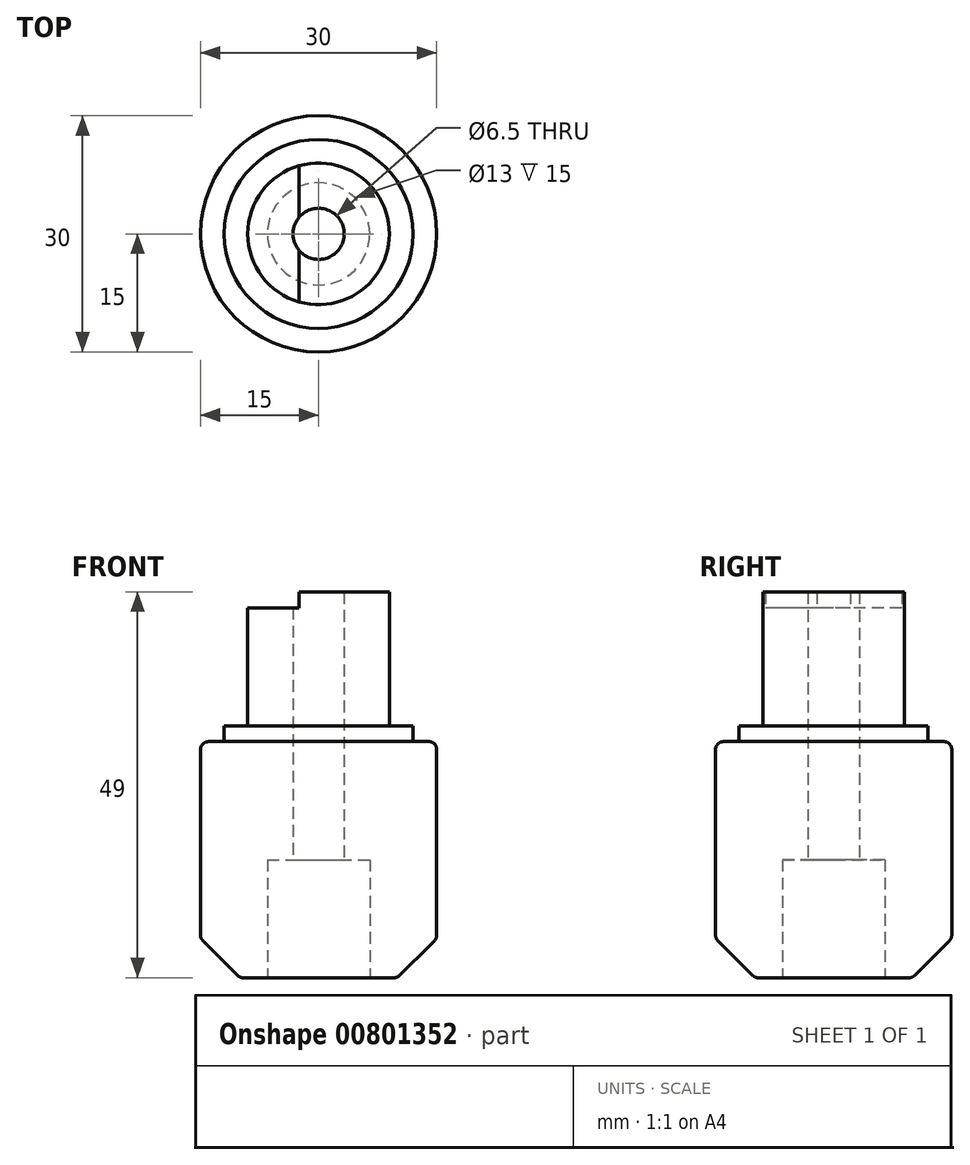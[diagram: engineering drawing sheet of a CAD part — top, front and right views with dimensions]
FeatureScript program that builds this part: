
annotation { "Feature Type Name" : "Feature", "Feature Type Description" : "" }
export const myFeature = defineFeature(function(context is Context, id is Id, definition is map)
    precondition{}
    {
        {
            var Q0;
            Q0=qCreatedBy(makeId("Top.planeOp"),FACE);
            var sketch = newSketch(context, id + "F0", { "sketchPlane" : qUnion([Q0])});
            skCircle(sketch, "E0", {"center": v(0, 0) * mm, "radius": 15 * mm});
            skSolve(sketch);
        }
        {
            var Q0;
            Q0=makeQuery(id+"F0.imprint","IMPRINT",FACE,{"disambiguationData":[TD([[makeQuery(id+"F0.imprint","IMPRINT",EDGE,{"derivedFrom":sQuery(id+"F0.wireOp",EDGE,"E0")}),1.0]])]});
            extrude(context, id + "F1", {"entities" : qUnion([Q0]), "depth" : 30 * mm, "offsetDistance" : 25 * mm});
        }
        {
            var Q0;
            Q0=makeQuery(id+"F1.opExtrude","CAP_FACE",FACE,{"disambiguationData":[OSD([sQuery(id+"F0.wireOp",EDGE,"E0")])],"isStart":false});
            var sketch = newSketch(context, id + "F2", { "sketchPlane" : qUnion([Q0])});
            skCircle(sketch, "E1", {"center": v(0, 0) * mm, "radius": 12 * mm});
            skSolve(sketch);
        }
        {
            var Q0;
            Q0=makeQuery(id+"F2.imprint","IMPRINT",FACE,{"disambiguationData":[TD([[makeQuery(id+"F2.imprint","IMPRINT",EDGE,{"derivedFrom":sQuery(id+"F2.wireOp",EDGE,"E1")}),1.0]])]});
            extrude(context, id + "F3", {"entities" : qUnion([Q0]), "operationType" : NewBodyOperationType.ADD, "depth" : 2 * mm, "offsetDistance" : 25 * mm});
        }
        {
            var Q0;
            Q0=makeQuery(id+"F3.opExtrude","CAP_FACE",FACE,{"disambiguationData":[OSD([sQuery(id+"F2.wireOp",EDGE,"E1")])],"isStart":false});
            var sketch = newSketch(context, id + "F4", { "sketchPlane" : qUnion([Q0])});
            skCircle(sketch, "E2", {"center": v(0, 0) * mm, "radius": 9 * mm});
            skLineSegment(sketch, "E3", {"start": v(-2.47, 8.66) * mm, "end": v(-2.47, -8.66) * mm});
            skSolve(sketch);
        }
        {
            var Q0;
            {var subQ0=sQuery(id+"F4.wireOp",EDGE,"E3");Q0=makeQuery(id+"F4.imprint","IMPRINT",FACE,{"disambiguationData":[TD([[makeQuery(id+"F4.imprint","IMPRINT",EDGE,{"derivedFrom":subQ0}),1.0]])]});}
            extrude(context, id + "F5", {"entities" : qUnion([Q0]), "operationType" : NewBodyOperationType.ADD, "depth" : 17 * mm, "offsetDistance" : 25 * mm});
        }
        {
            var Q0;
            {var subQ0=sQuery(id+"F4.wireOp",EDGE,"E3");Q0=makeQuery(id+"F4.imprint","IMPRINT",FACE,{"disambiguationData":[TD([[makeQuery(id+"F4.imprint","IMPRINT",EDGE,{"derivedFrom":subQ0}),-1.0]])]});}
            extrude(context, id + "F6", {"entities" : qUnion([Q0]), "operationType" : NewBodyOperationType.ADD, "depth" : 15 * mm, "offsetDistance" : 25 * mm});
        }
        {
            var Q0;
            Q0=sQuery(id+"F0.wireOp",VERTEX,"E0.center");
            var Q1;
            Q1=makeQuery(id+"F1.opExtrude","SWEPT_BODY",BODY,{"disambiguationData":[OSD([sQuery(id+"F0.wireOp",EDGE,"E0")])]});
            hole(context, id + "F7", {"style" : HoleStyle.C_BORE, "endStyle" : HoleEndStyle.THROUGH, "oppositeDirection" : true, "holeDiameter" : 6.5 * mm, "cBoreDiameter" : 13 * mm, "cBoreDepth" : 15 * mm, "majorDiameter" : 5 * mm, "isTappedThrough" : true, "tappedDepth" : 12 * mm, "tapClearance" : 3, "locations" : qUnion([Q0]), "scope" : qUnion([Q1])});
        }
        {
            var Q0;
            Q0=makeQuery(id+"F1.opExtrude","CAP_EDGE",EDGE,{"disambiguationData":[OSD([sQuery(id+"F0.wireOp",EDGE,"E0")])],"isStart":true});
            chamfer(context, id + "F8", {"entities" : qUnion([Q0]), "width" : 5 * mm, "tangentPropagation" : true});
        }
        {
            var Q0;
            Q0=makeQuery(id+"F7.hole-0.boolean.opBoolean","COPY",EDGE,{"derivedFrom":makeQuery(id+"F7.hole-0.opRevolve","SWEPT_EDGE",EDGE,{"disambiguationData":[OSD([sQuery(id+"F7.hole-0.sketch.wireOp",EDGE,"cbore_start_line_2"),sQuery(id+"F7.hole-0.sketch.wireOp",EDGE,"cbore_start_line_3")])]})});
            var Q1;
            Q1=makeQuery(id+"F1.opExtrude","CAP_EDGE",EDGE,{"disambiguationData":[OSD([sQuery(id+"F0.wireOp",EDGE,"E0")])],"isStart":false});
            var Q2;
            {var subQ0=sQuery(id+"F0.wireOp",EDGE,"E0");Q2=makeQuery(id+"F8.opChamfer","BLEND_EDGE",EDGE,{"blendedFrom":[makeQuery(id+"F1.opExtrude","CAP_EDGE",EDGE,{"disambiguationData":[OSD([subQ0])],"isStart":true}),makeQuery(id+"F1.opExtrude","CAP_FACE",FACE,{"disambiguationData":[OSD([subQ0])],"isStart":true})],"blendedInto":[makeQuery(id+"F1.opExtrude","CAP_FACE",FACE,{"disambiguationData":[OSD([subQ0])],"isStart":true})]});}
            var Q3;
            {var subQ0=sQuery(id+"F0.wireOp",EDGE,"E0");Q3=makeQuery(id+"F8.opChamfer","BLEND_EDGE",EDGE,{"blendedFrom":[makeQuery(id+"F1.opExtrude","CAP_EDGE",EDGE,{"disambiguationData":[OSD([subQ0])],"isStart":true}),makeQuery(id+"F1.opExtrude","SWEPT_FACE",FACE,{"disambiguationData":[OSD([subQ0])]})],"blendedInto":[makeQuery(id+"F1.opExtrude","SWEPT_FACE",FACE,{"disambiguationData":[OSD([subQ0])]})]});}
            fillet(context, id + "F9", {"entities" : qUnion([Q0, Q1, Q2, Q3]), "radius" : 1 * mm, "tangentPropagation" : true, "allowEdgeOverflow" : false});
        }
    });
